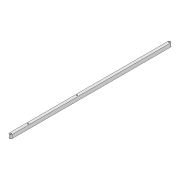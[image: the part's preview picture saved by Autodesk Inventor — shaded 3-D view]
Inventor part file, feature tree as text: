
AUTODESK INVENTOR PART (.ipt)
format: ipt  version: 2022 (Build 260153000, 153)  size: 92,160 bytes
history: native  units: mm
features: extrude x1, sketch x1
ambient origin geometry x8: Origin, YZ Plane, XZ Plane, XY Plane, X Axis, Y Axis, Z Axis, Center Point
bodies: Solid1 (feature_tree)
feature tree (2):
  extrude  "Extrusion1"  Depth=6.0mm
  sketch  "Sketch1"  dims[d0=347.765mm d1=6.0mm d2=3.0mm d3=3.0mm d4=8.0mm d5=0.0mm d6=3.0mm d7=145.527mm d8=3.0mm d9=37.934mm]
